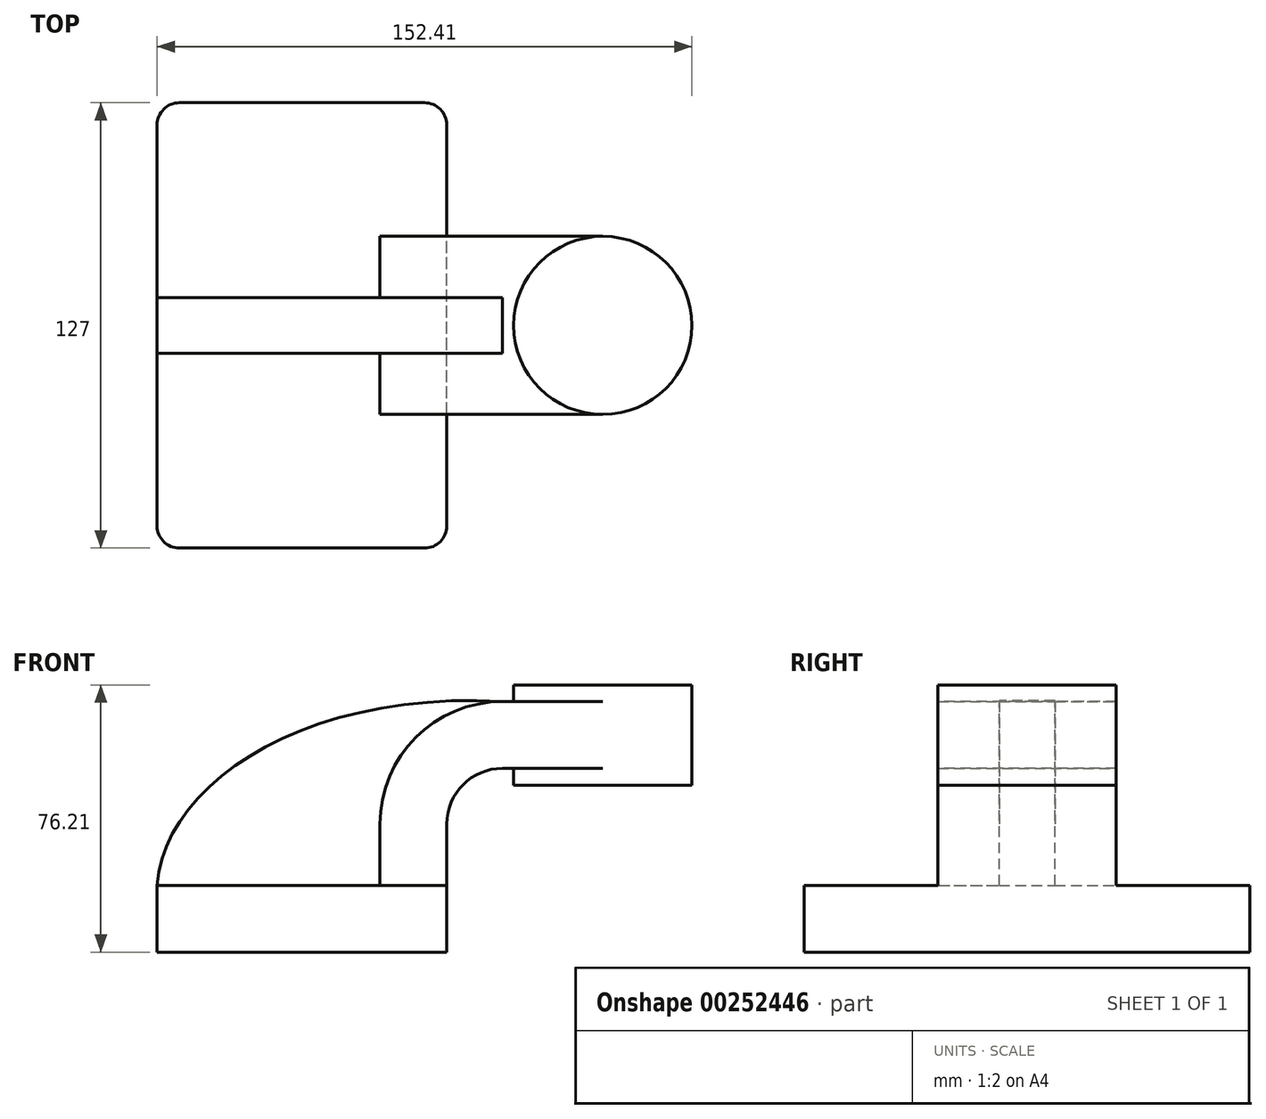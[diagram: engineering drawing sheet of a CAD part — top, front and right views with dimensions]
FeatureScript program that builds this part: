
annotation { "Feature Type Name" : "Feature", "Feature Type Description" : "" }
export const myFeature = defineFeature(function(context is Context, id is Id, definition is map)
    precondition{}
    {
        {
            var Q0;
            Q0=qCreatedBy(makeId("Front.planeOp"),FACE);
            var sketch = newSketch(context, id + "F0", { "sketchPlane" : qUnion([Q0])});
            skLineSegment(sketch, "E0.bottom", {"start": v(-41.28, 9.52) * mm, "end": v(41.28, 9.52) * mm});
            skLineSegment(sketch, "E0.top", {"start": v(-41.28, -9.52) * mm, "end": v(41.28, -9.52) * mm});
            skLineSegment(sketch, "E0.left", {"start": v(-41.28, 9.52) * mm, "end": v(-41.28, -9.52) * mm});
            skLineSegment(sketch, "E0.right", {"start": v(41.28, 9.52) * mm, "end": v(41.28, -9.52) * mm});
            skPoint(sketch, "E0.middle", {"position": v(0, 0) * mm});
            skLineSegment(sketch, "E1.bottom", {"start": v(60.32, 38.1) * mm, "end": v(111.12, 38.1) * mm});
            skLineSegment(sketch, "E1.top", {"start": v(60.32, 66.68) * mm, "end": v(111.12, 66.68) * mm});
            skLineSegment(sketch, "E1.left", {"start": v(60.32, 38.1) * mm, "end": v(60.32, 66.68) * mm});
            skLineSegment(sketch, "E1.right", {"start": v(111.12, 38.1) * mm, "end": v(111.12, 66.68) * mm});
            skPoint(sketch, "E1.middle", {"position": v(85.72, 52.39) * mm});
            skLineSegment(sketch, "E2", {"start": v(41.28, 9.52) * mm, "end": v(41.28, 27) * mm});
            skArc(sketch, "E3", {"start": v(41.28, 27) * mm, "mid": v(45.92, 38.23) * mm, "end": v(57.15, 42.88) * mm});
            skLineSegment(sketch, "E4", {"start": v(57.15, 42.88) * mm, "end": v(85.72, 42.88) * mm});
            skPoint(sketch, "E4.endSnap0", {"position": v(85.72, 38.1) * mm});
            skLineSegment(sketch, "E5.0", {"start": v(22.23, 9.52) * mm, "end": v(22.23, 27) * mm});
            skArc(sketch, "E6.0", {"start": v(22.23, 27) * mm, "mid": v(32.45, 51.7) * mm, "end": v(57.15, 61.93) * mm});
            skLineSegment(sketch, "E7.0", {"start": v(57.15, 61.93) * mm, "end": v(85.72, 61.93) * mm});
            skLineSegment(sketch, "E8", {"start": v(85.72, 66.68) * mm, "end": v(85.72, 38.1) * mm});
            skFitSpline(sketch, "E9", {"points": [v(-41.28, 9.52) * mm, v(57.15, 61.93) * mm], "startDerivative": vector(6.08, 85.7) * mm, "endDerivative": vector(171.45, -9.89) * mm});
            skSolve(sketch);
        }
        {
            var Q0;
            Q0=makeQuery(id+"F0.imprint","IMPRINT",FACE,{"disambiguationData":[TD([[makeQuery(id+"F0.imprint","IMPRINT",EDGE,{"derivedFrom":sQuery(id+"F0.wireOp",EDGE,"E0.top")}),1.0]])]});
            extrude(context, id + "F1", {"entities" : qUnion([Q0]), "endBound" : BoundingType.SYMMETRIC, "depth" : 127 * mm});
        }
        {
            var Q0;
            {var subQ2=sQuery(id+"F0.wireOp",EDGE,"E2");Q0=makeQuery(id+"F0.imprint","IMPRINT",FACE,{"disambiguationData":[TD([[makeQuery(id+"F0.imprint","IMPRINT",EDGE,{"derivedFrom":subQ2}),1.0]])]});}
            var Q1;
            {var subQ0=sQuery(id+"F0.wireOp",EDGE,"E4");var subQ1=sQuery(id+"F0.wireOp",EDGE,"E1.left");var subQ2=makeQuery(id+"F0.imprint","INTERSECT",VERTEX,{"derivedFrom":[subQ1,subQ0]});Q1=makeQuery(id+"F0.imprint","IMPRINT",FACE,{"disambiguationData":[TD([[makeQuery(id+"F0.imprint","IMPRINT",EDGE,{"disambiguationData":[TD([[subQ2,-1.0]])],"derivedFrom":subQ1}),-1.0]])]});}
            extrude(context, id + "F2", {"entities" : qUnion([Q0, Q1]), "operationType" : NewBodyOperationType.ADD, "endBound" : BoundingType.SYMMETRIC, "depth" : 50.8 * mm});
        }
        {
            var Q0;
            {var subQ2=sQuery(id+"F0.wireOp",EDGE,"E5.0");Q0=makeQuery(id+"F0.imprint","IMPRINT",FACE,{"disambiguationData":[TD([[makeQuery(id+"F0.imprint","IMPRINT",EDGE,{"derivedFrom":subQ2}),1.0]])]});}
            extrude(context, id + "F3", {"entities" : qUnion([Q0]), "operationType" : NewBodyOperationType.ADD, "endBound" : BoundingType.SYMMETRIC, "depth" : 15.88 * mm});
        }
        {
            var Q0;
            {var subQ0=sQuery(id+"F0.wireOp",EDGE,"E1.right");Q0=makeQuery(id+"F0.imprint","IMPRINT",FACE,{"disambiguationData":[TD([[makeQuery(id+"F0.imprint","IMPRINT",EDGE,{"derivedFrom":subQ0}),1.0]])]});}
            var Q1;
            Q1=sQuery(id+"F0.wireOp",EDGE,"E8");
            revolve(context, id + "F4", {"operationType" : NewBodyOperationType.ADD, "entities" : qUnion([Q0]), "axis" : qUnion([Q1]), "revolveType" : RevolveType.FULL});
        }
        {
            var Q0;
            Q0=makeQuery(id+"F1.opExtrude","CAP_EDGE",EDGE,{"disambiguationData":[OSD([sQuery(id+"F0.wireOp",EDGE,"E0.right")])],"isStart":false});
            var Q1;
            Q1=makeQuery(id+"F1.opExtrude","CAP_EDGE",EDGE,{"disambiguationData":[OSD([sQuery(id+"F0.wireOp",EDGE,"E0.left")])],"isStart":false});
            var Q2;
            Q2=makeQuery(id+"F1.opExtrude","CAP_EDGE",EDGE,{"disambiguationData":[OSD([sQuery(id+"F0.wireOp",EDGE,"E0.left")])],"isStart":true});
            var Q3;
            Q3=makeQuery(id+"F1.opExtrude","CAP_EDGE",EDGE,{"disambiguationData":[OSD([sQuery(id+"F0.wireOp",EDGE,"E0.right")])],"isStart":true});
            fillet(context, id + "F5", {"entities" : qUnion([Q0, Q1, Q2, Q3]), "radius" : 6.35 * mm, "tangentPropagation" : true, "allowEdgeOverflow" : false});
        }
    });
